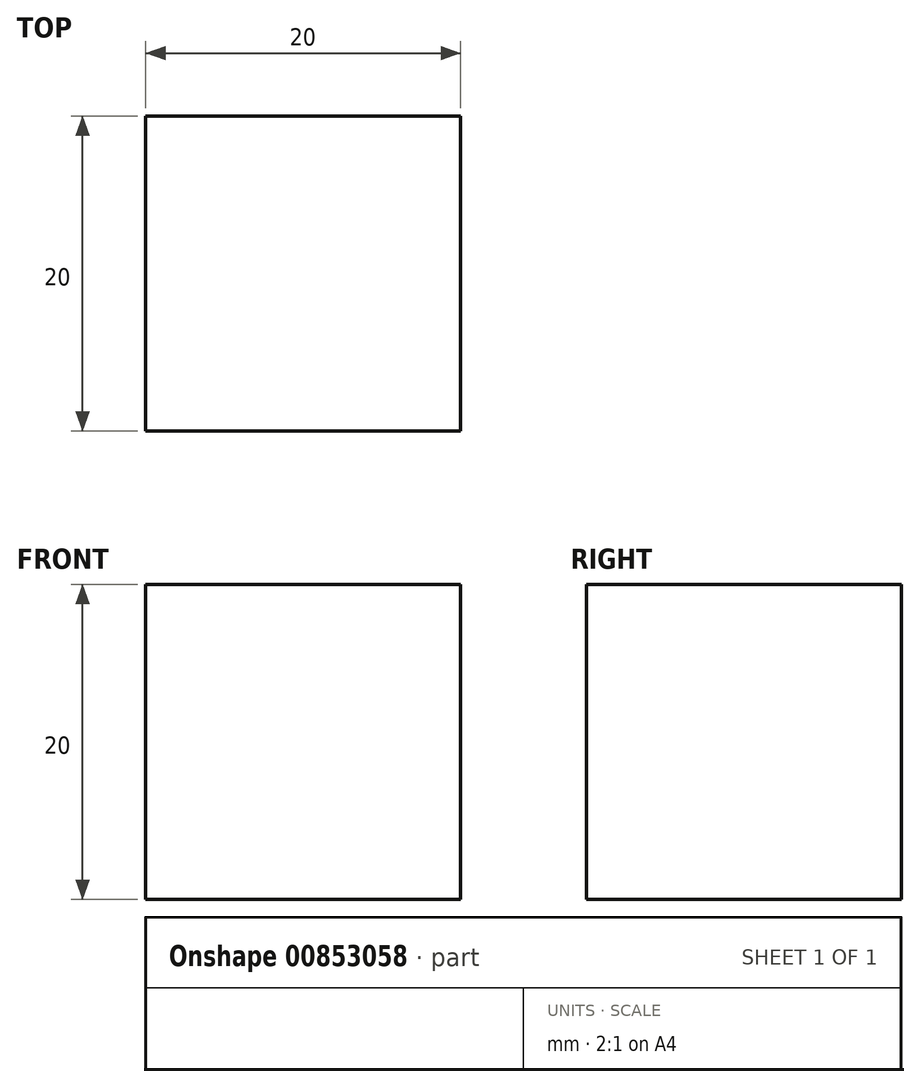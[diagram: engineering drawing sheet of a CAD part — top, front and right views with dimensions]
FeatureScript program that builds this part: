
annotation { "Feature Type Name" : "Feature", "Feature Type Description" : "" }
export const myFeature = defineFeature(function(context is Context, id is Id, definition is map)
    precondition{}
    {
        {
            var Q0;
            Q0=qCreatedBy(makeId("Front.planeOp"),FACE);
            var sketch = newSketch(context, id + "F0", { "sketchPlane" : qUnion([Q0])});
            skLineSegment(sketch, "E0.bottom", {"start": v(0, 0) * mm, "end": v(20, 0) * mm});
            skLineSegment(sketch, "E0.top", {"start": v(0, 20) * mm, "end": v(20, 20) * mm});
            skLineSegment(sketch, "E0.left", {"start": v(0, 0) * mm, "end": v(0, 20) * mm});
            skLineSegment(sketch, "E0.right", {"start": v(20, 0) * mm, "end": v(20, 20) * mm});
            skSolve(sketch);
        }
        {
            var Q0;
            Q0=makeQuery(id+"F0.imprint","IMPRINT",FACE,{"disambiguationData":[TD([[makeQuery(id+"F0.imprint","IMPRINT",EDGE,{"derivedFrom":sQuery(id+"F0.wireOp",EDGE,"E0.bottom")}),1.0]])]});
            extrude(context, id + "F1", {"entities" : qUnion([Q0]), "depth" : 20 * mm, "offsetDistance" : 25 * mm});
        }
    });
